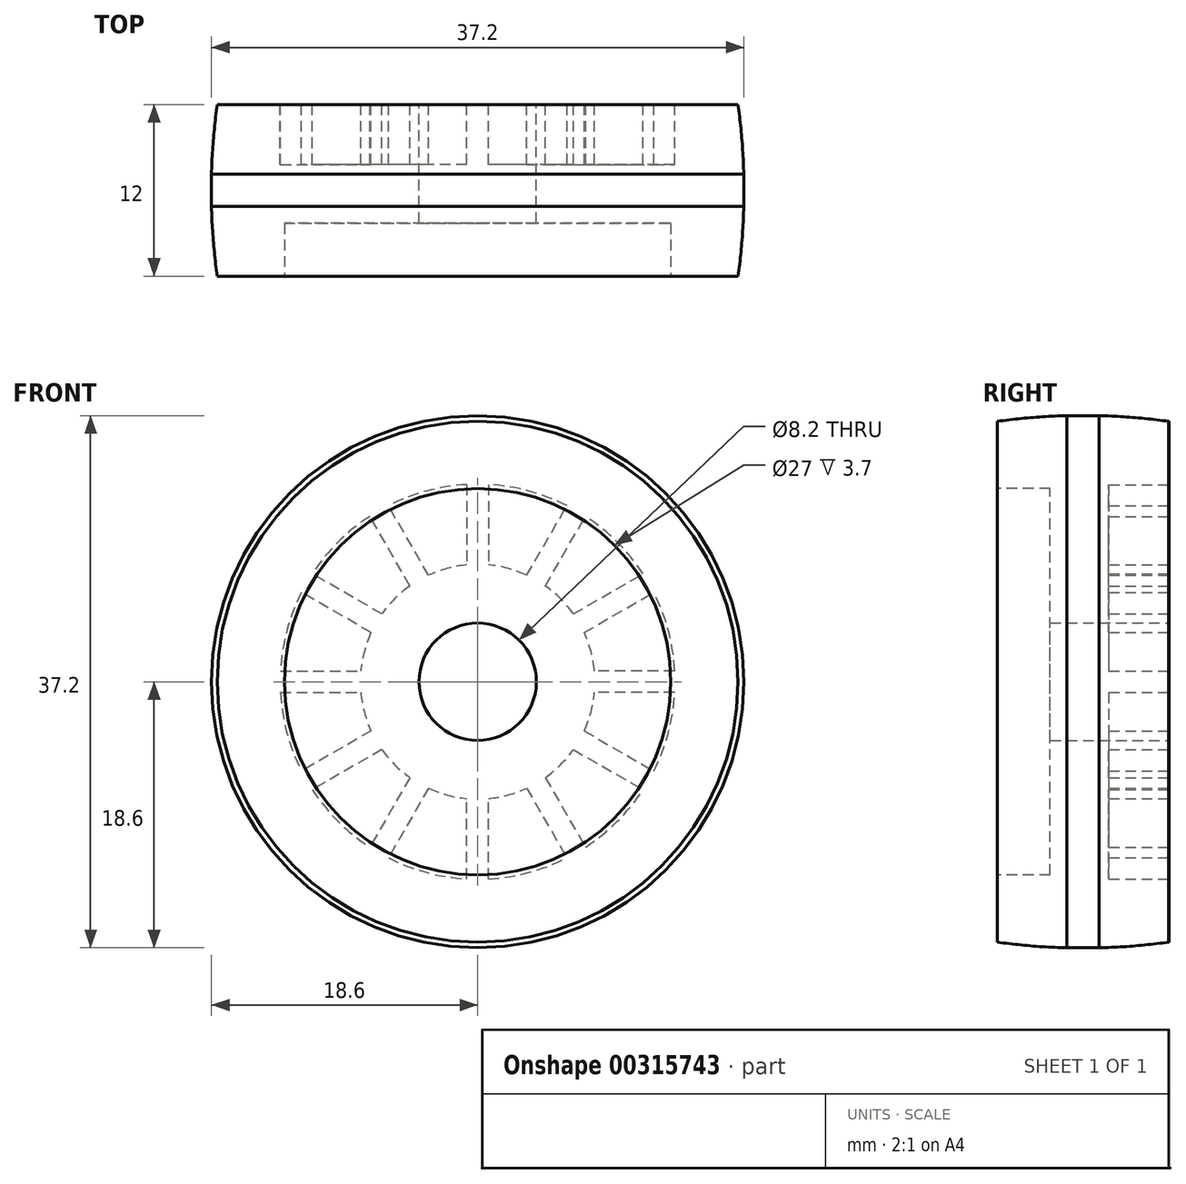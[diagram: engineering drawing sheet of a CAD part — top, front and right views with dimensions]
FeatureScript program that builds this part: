
annotation { "Feature Type Name" : "Feature", "Feature Type Description" : "" }
export const myFeature = defineFeature(function(context is Context, id is Id, definition is map)
    precondition{}
    {
        {
            var Q0;
            Q0=qCreatedBy(makeId("Front.planeOp"),FACE);
            var sketch = newSketch(context, id + "F0", { "sketchPlane" : qUnion([Q0])});
            skCircle(sketch, "E0", {"center": v(0, 0) * mm, "radius": 18.6 * mm});
            skCircle(sketch, "E1", {"center": v(0, 0) * mm, "radius": 4.1 * mm});
            skSolve(sketch);
        }
        {
            var Q0;
            Q0=makeQuery(id+"F0.imprint","IMPRINT",FACE,{"disambiguationData":[TD([[makeQuery(id+"F0.imprint","IMPRINT",EDGE,{"derivedFrom":sQuery(id+"F0.wireOp",EDGE,"E0")}),1.0]])]});
            extrude(context, id + "F1", {"entities" : qUnion([Q0]), "depth" : 12 * mm});
        }
        {
            var Q0;
            Q0=makeQuery(id+"F1.opExtrude","CAP_FACE",FACE,{"disambiguationData":[OSD([sQuery(id+"F0.wireOp",EDGE,"E0"),sQuery(id+"F0.wireOp",EDGE,"E1")])],"isStart":false});
            var sketch = newSketch(context, id + "F2", { "sketchPlane" : qUnion([Q0])});
            skCircle(sketch, "E2", {"center": v(0, 0) * mm, "radius": 13.5 * mm});
            skSolve(sketch);
        }
        {
            var Q0;
            Q0=makeQuery(id+"F2.imprint","IMPRINT",FACE,{"disambiguationData":[TD([[makeQuery(id+"F2.imprint","IMPRINT",EDGE,{"derivedFrom":sQuery(id+"F2.wireOp",EDGE,"E2")}),1.0]])]});
            extrude(context, id + "F3", {"entities" : qUnion([Q0]), "operationType" : NewBodyOperationType.REMOVE, "oppositeDirection" : true, "depth" : 3.7 * mm});
        }
        {
            var Q0;
            Q0=makeQuery(id+"F1.opExtrude","CAP_FACE",FACE,{"disambiguationData":[OSD([sQuery(id+"F0.wireOp",EDGE,"E0"),sQuery(id+"F0.wireOp",EDGE,"E1")])],"isStart":true});
            var sketch = newSketch(context, id + "F4", { "sketchPlane" : qUnion([Q0])});
            skArc(sketch, "E3", {"start": v(-12.3, 6.24) * mm, "mid": v(-13.33, 3.57) * mm, "end": v(-13.78, 0.75) * mm});
            skArc(sketch, "E4", {"start": v(-7.45, 3.43) * mm, "mid": v(-7.92, 2.12) * mm, "end": v(-8.17, 0.74) * mm});
            skPoint(sketch, "E5.orphan", {"position": v(-9.95, 17.24) * mm});
            skPoint(sketch, "E6.orphan", {"position": v(0, 19.87) * mm});
            skPoint(sketch, "E7.orphan", {"position": v(9.95, 17.24) * mm});
            skPoint(sketch, "E8.orphan", {"position": v(17.35, 10.02) * mm});
            skPoint(sketch, "E9.orphan", {"position": v(17.35, -10.02) * mm});
            skPoint(sketch, "E10.orphan", {"position": v(9.95, -17.24) * mm});
            skPoint(sketch, "E11.orphan", {"position": v(-9.95, -17.24) * mm});
            skPoint(sketch, "E12.orphan", {"position": v(-17.35, -10.02) * mm});
            skPoint(sketch, "E13.orphan", {"position": v(-17.35, 10.02) * mm});
            skLineSegment(sketch, "E14.0", {"start": v(-0.75, 13.8) * mm, "end": v(-0.75, 8.17) * mm});
            skLineSegment(sketch, "E15.0", {"start": v(0.75, 13.8) * mm, "end": v(0.75, 8.17) * mm});
            skLineSegment(sketch, "E16.0", {"start": v(4.73, 6.7) * mm, "end": v(7.55, 11.58) * mm});
            skLineSegment(sketch, "E17.0", {"start": v(3.44, 7.44) * mm, "end": v(6.25, 12.33) * mm});
            skLineSegment(sketch, "E18.0", {"start": v(7.45, 3.43) * mm, "end": v(12.33, 6.25) * mm});
            skLineSegment(sketch, "E19.0", {"start": v(6.7, 4.74) * mm, "end": v(11.58, 7.55) * mm});
            skPoint(sketch, "E20.orphan", {"position": v(20.13, 0) * mm});
            skLineSegment(sketch, "E21.0", {"start": v(13.8, 0.75) * mm, "end": v(8.17, 0.74) * mm});
            skLineSegment(sketch, "E22.0", {"start": v(13.8, -0.75) * mm, "end": v(13.78, -0.75) * mm});
            skLineSegment(sketch, "E23.MirrorCS", {"start": v(-3.44, 7.44) * mm, "end": v(-6.25, 12.33) * mm});
            skLineSegment(sketch, "E24.MirrorCS", {"start": v(-4.73, 6.7) * mm, "end": v(-7.55, 11.58) * mm});
            skLineSegment(sketch, "E25.MirrorCS", {"start": v(-6.7, 4.74) * mm, "end": v(-11.58, 7.55) * mm});
            skLineSegment(sketch, "E26.MirrorCS", {"start": v(-7.45, 3.43) * mm, "end": v(-12.33, 6.25) * mm});
            skLineSegment(sketch, "E27.MirrorCS", {"start": v(-13.8, 0.75) * mm, "end": v(-8.17, 0.74) * mm});
            skLineSegment(sketch, "E28.MirrorCS", {"start": v(-13.8, -0.75) * mm, "end": v(-8.17, -0.74) * mm});
            skLineSegment(sketch, "E29.MirrorCS", {"start": v(-7.45, -3.43) * mm, "end": v(-12.33, -6.25) * mm});
            skLineSegment(sketch, "E30.MirrorCS", {"start": v(-6.7, -4.74) * mm, "end": v(-11.58, -7.55) * mm});
            skLineSegment(sketch, "E31.MirrorCS", {"start": v(-4.73, -6.7) * mm, "end": v(-7.55, -11.58) * mm});
            skLineSegment(sketch, "E32.MirrorCS", {"start": v(-3.44, -7.44) * mm, "end": v(-6.25, -12.33) * mm});
            skLineSegment(sketch, "E33.MirrorCS", {"start": v(-0.75, -13.8) * mm, "end": v(-0.75, -8.17) * mm});
            skLineSegment(sketch, "E34.MirrorCS", {"start": v(0.75, -13.8) * mm, "end": v(0.75, -8.17) * mm});
            skLineSegment(sketch, "E35.MirrorCS", {"start": v(3.44, -7.44) * mm, "end": v(6.25, -12.33) * mm});
            skLineSegment(sketch, "E36.MirrorCS", {"start": v(4.73, -6.7) * mm, "end": v(7.55, -11.58) * mm});
            skLineSegment(sketch, "E37.MirrorCS", {"start": v(6.7, -4.74) * mm, "end": v(11.58, -7.55) * mm});
            skLineSegment(sketch, "E38.MirrorCS", {"start": v(7.45, -3.43) * mm, "end": v(12.33, -6.25) * mm});
            skLineSegment(sketch, "E39.MirrorCS", {"start": v(13.8, -0.75) * mm, "end": v(8.17, -0.74) * mm});
            skPoint(sketch, "E40.start.orphan", {"position": v(0, 15.5) * mm});
            skPoint(sketch, "E41.start.orphan", {"position": v(15.8, 0) * mm});
            skArc(sketch, "E42.trimOffspring", {"start": v(-4.73, 6.7) * mm, "mid": v(-5.8, 5.8) * mm, "end": v(-6.7, 4.74) * mm});
            skArc(sketch, "E43.trimOffspring", {"start": v(-7.54, 11.56) * mm, "mid": v(-9.76, 9.76) * mm, "end": v(-11.56, 7.54) * mm});
            skArc(sketch, "E44.trimOffspring", {"start": v(-0.75, 13.78) * mm, "mid": v(-3.57, 13.33) * mm, "end": v(-6.24, 12.3) * mm});
            skArc(sketch, "E45.trimOffspring", {"start": v(-0.75, 8.17) * mm, "mid": v(-2.12, 7.92) * mm, "end": v(-3.44, 7.44) * mm});
            skArc(sketch, "E46.trimOffspring", {"start": v(3.44, 7.44) * mm, "mid": v(2.12, 7.92) * mm, "end": v(0.75, 8.17) * mm});
            skArc(sketch, "E47.trimOffspring", {"start": v(6.24, 12.3) * mm, "mid": v(3.57, 13.33) * mm, "end": v(0.75, 13.78) * mm});
            skArc(sketch, "E48.trimOffspring", {"start": v(11.56, 7.54) * mm, "mid": v(9.76, 9.76) * mm, "end": v(7.54, 11.56) * mm});
            skArc(sketch, "E49.trimOffspring", {"start": v(6.7, 4.74) * mm, "mid": v(5.8, 5.8) * mm, "end": v(4.73, 6.7) * mm});
            skArc(sketch, "E50.trimOffspring", {"start": v(8.17, 0.74) * mm, "mid": v(7.92, 2.12) * mm, "end": v(7.45, 3.43) * mm});
            skArc(sketch, "E51.trimOffspring", {"start": v(13.78, 0.75) * mm, "mid": v(13.33, 3.57) * mm, "end": v(12.3, 6.24) * mm});
            skArc(sketch, "E52.trimOffspring", {"start": v(7.45, -3.43) * mm, "mid": v(7.92, -2.12) * mm, "end": v(8.17, -0.74) * mm});
            skArc(sketch, "E53.trimOffspring", {"start": v(12.3, -6.24) * mm, "mid": v(13.33, -3.57) * mm, "end": v(13.78, -0.75) * mm});
            skArc(sketch, "E54.trimOffspring", {"start": v(7.54, -11.56) * mm, "mid": v(9.76, -9.76) * mm, "end": v(11.56, -7.54) * mm});
            skArc(sketch, "E55.trimOffspring", {"start": v(4.73, -6.7) * mm, "mid": v(5.8, -5.8) * mm, "end": v(6.7, -4.74) * mm});
            skArc(sketch, "E56.trimOffspring", {"start": v(0.75, -8.17) * mm, "mid": v(2.12, -7.92) * mm, "end": v(3.44, -7.44) * mm});
            skArc(sketch, "E57.trimOffspring", {"start": v(0.75, -13.78) * mm, "mid": v(3.57, -13.33) * mm, "end": v(6.24, -12.3) * mm});
            skArc(sketch, "E58.trimOffspring", {"start": v(-3.44, -7.44) * mm, "mid": v(-2.12, -7.92) * mm, "end": v(-0.75, -8.17) * mm});
            skArc(sketch, "E59.trimOffspring", {"start": v(-6.24, -12.3) * mm, "mid": v(-3.57, -13.33) * mm, "end": v(-0.75, -13.78) * mm});
            skArc(sketch, "E60.trimOffspring", {"start": v(-11.56, -7.54) * mm, "mid": v(-9.76, -9.76) * mm, "end": v(-7.54, -11.56) * mm});
            skArc(sketch, "E61.trimOffspring", {"start": v(-6.7, -4.74) * mm, "mid": v(-5.8, -5.8) * mm, "end": v(-4.73, -6.7) * mm});
            skArc(sketch, "E62.trimOffspring", {"start": v(-8.17, -0.74) * mm, "mid": v(-7.92, -2.12) * mm, "end": v(-7.45, -3.43) * mm});
            skArc(sketch, "E63.trimOffspring", {"start": v(-13.78, -0.75) * mm, "mid": v(-13.33, -3.57) * mm, "end": v(-12.3, -6.24) * mm});
            skSolve(sketch);
        }
        {
            var Q0;
            Q0 = qSketchRegion(id + "F4", true);
            extrude(context, id + "F5", {"entities" : qUnion([Q0]), "operationType" : NewBodyOperationType.REMOVE, "oppositeDirection" : true, "depth" : 4.2 * mm});
        }
        {
            var Q0;
            Q0=qCreatedBy(makeId("Right.planeOp"),FACE);
            var sketch = newSketch(context, id + "F6", { "sketchPlane" : qUnion([Q0])});
            skLineSegment(sketch, "E64", {"start": v(-16.06, 0) * mm, "end": v(10.98, 0) * mm});
            skArc(sketch, "E65", {"start": v(0, 18.2) * mm, "mid": v(-6, 18.61) * mm, "end": v(-12, 18.2) * mm});
            skLineSegment(sketch, "E66", {"start": v(-12, 18.2) * mm, "end": v(-12.28, 18.16) * mm});
            skLineSegment(sketch, "E67", {"start": v(-12.28, 18.16) * mm, "end": v(-12.28, 18.6) * mm});
            skLineSegment(sketch, "E68", {"start": v(0.37, 18.6) * mm, "end": v(0.37, 18.16) * mm});
            skLineSegment(sketch, "E69", {"start": v(0.37, 18.16) * mm, "end": v(0, 18.2) * mm});
            skLineSegment(sketch, "E70", {"start": v(-12.28, 18.6) * mm, "end": v(-12.3, 19.19) * mm});
            skLineSegment(sketch, "E71", {"start": v(-12.3, 19.19) * mm, "end": v(0.36, 19.19) * mm});
            skLineSegment(sketch, "E72", {"start": v(0.36, 19.19) * mm, "end": v(0.37, 18.6) * mm});
            skPoint(sketch, "E73.end.orphan", {"position": v(-12, 18.6) * mm});
            skPoint(sketch, "E74.start.orphan", {"position": v(0, 18.6) * mm});
            skSolve(sketch);
        }
        {
            var Q0;
            Q0=makeQuery(id+"F6.imprint","IMPRINT",FACE,{"disambiguationData":[TD([[makeQuery(id+"F6.imprint","IMPRINT",EDGE,{"derivedFrom":sQuery(id+"F6.wireOp",EDGE,"E65")}),-1.0]])]});
            var Q1;
            Q1=sQuery(id+"F6.wireOp",EDGE,"E64");
            revolve(context, id + "F7", {"operationType" : NewBodyOperationType.REMOVE, "entities" : qUnion([Q0]), "axis" : qUnion([Q1]), "revolveType" : RevolveType.FULL, "oppositeDirection" : true});
        }
    });
